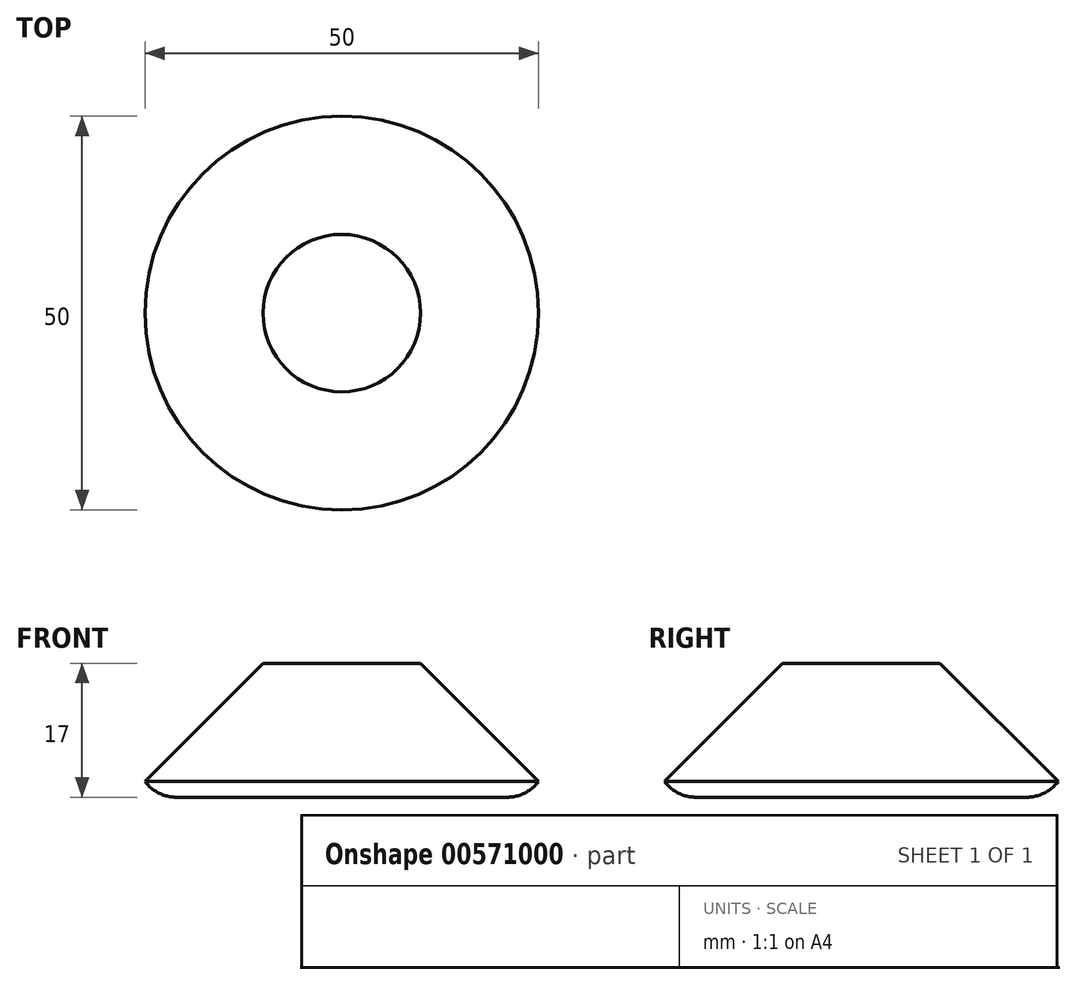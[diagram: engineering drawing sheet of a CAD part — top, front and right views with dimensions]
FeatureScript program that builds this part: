
annotation { "Feature Type Name" : "Feature", "Feature Type Description" : "" }
export const myFeature = defineFeature(function(context is Context, id is Id, definition is map)
    precondition{}
    {
        {
            var Q0;
            Q0=qCreatedBy(makeId("Top.planeOp"),FACE);
            var sketch = newSketch(context, id + "F0", { "sketchPlane" : qUnion([Q0])});
            skCircle(sketch, "E0", {"center": v(-14.68, 6.99) * mm, "radius": 25 * mm});
            skSolve(sketch);
        }
        {
            var Q0;
            Q0=makeQuery(id+"F0.imprint","IMPRINT",FACE,{"disambiguationData":[TD([[makeQuery(id+"F0.imprint","IMPRINT",EDGE,{"derivedFrom":sQuery(id+"F0.wireOp",EDGE,"E0")}),1.0]])]});
            extrude(context, id + "F1", {"entities" : qUnion([Q0]), "depth" : 17 * mm, "offsetDistance" : 25 * mm});
        }
        {
            var Q0;
            Q0=makeQuery(id+"F1.opExtrude","CAP_FACE",FACE,{"disambiguationData":[OSD([sQuery(id+"F0.wireOp",EDGE,"E0")])],"isStart":false});
            chamfer(context, id + "F2", {"entities" : qUnion([Q0]), "width" : 15 * mm, "tangentPropagation" : true});
        }
        {
            var Q0;
            Q0=makeQuery(id+"F1.opExtrude","CAP_EDGE",EDGE,{"disambiguationData":[OSD([sQuery(id+"F0.wireOp",EDGE,"E0")])],"isStart":true});
            fillet(context, id + "F3", {"entities" : qUnion([Q0]), "radius" : 5 * mm, "tangentPropagation" : true, "allowEdgeOverflow" : false});
        }
    });
